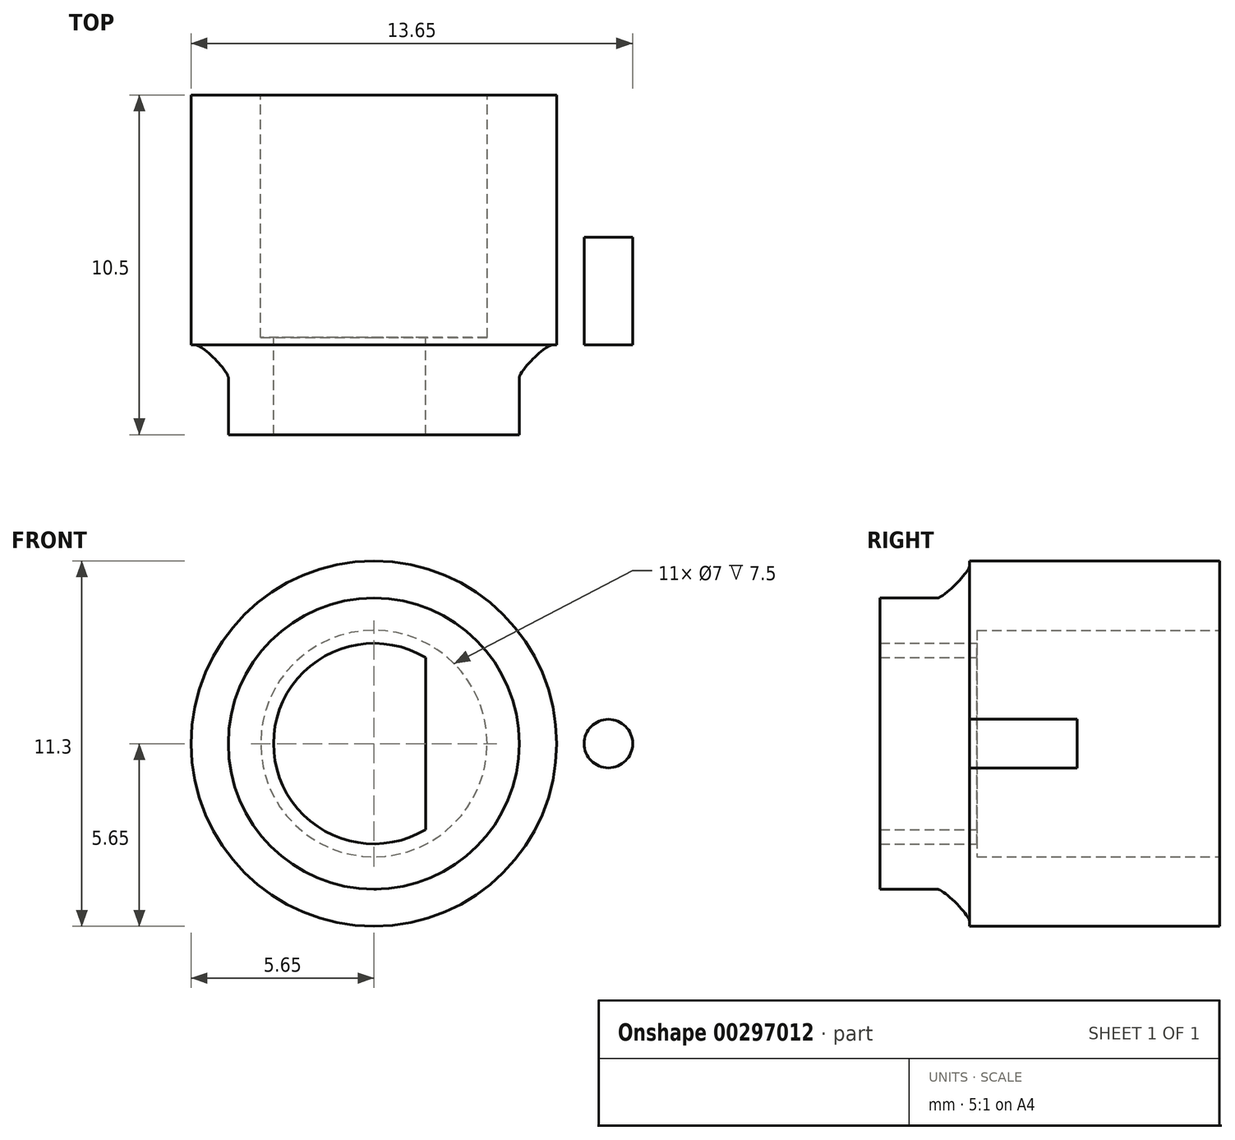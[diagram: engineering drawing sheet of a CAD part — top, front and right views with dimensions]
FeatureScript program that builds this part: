
annotation { "Feature Type Name" : "Feature", "Feature Type Description" : "" }
export const myFeature = defineFeature(function(context is Context, id is Id, definition is map)
    precondition{}
    {
        {
            var Q0;
            Q0=qCreatedBy(makeId("Top.planeOp"),FACE);
            var sketch = newSketch(context, id + "F0", { "sketchPlane" : qUnion([Q0])});
            skLineSegment(sketch, "E0", {"start": v(0, 7.73) * mm, "end": v(-5.65, 7.73) * mm});
            skLineSegment(sketch, "E1", {"start": v(-5.65, 7.73) * mm, "end": v(-5.65, 3.33) * mm});
            skLineSegment(sketch, "E2", {"start": v(-5.65, 3.33) * mm, "end": v(-9.35, 3.33) * mm});
            skLineSegment(sketch, "E3", {"start": v(-9.35, 3.33) * mm, "end": v(-9.35, 0) * mm});
            skLineSegment(sketch, "E4", {"start": v(-9.35, 0) * mm, "end": v(-4.5, 0) * mm});
            skLineSegment(sketch, "E5", {"start": v(-4.5, 0) * mm, "end": v(-4.5, -2.77) * mm});
            skLineSegment(sketch, "E6", {"start": v(-4.5, -2.77) * mm, "end": v(0, -2.77) * mm});
            skLineSegment(sketch, "E7", {"start": v(0, -2.77) * mm, "end": v(0, 7.73) * mm});
            skLineSegment(sketch, "E8", {"start": v(0, 7.73) * mm, "end": v(0, 5.8) * mm, "construction": true});
            skSolve(sketch);
        }
        {
            var Q0;
            {var subQ0=sQuery(id+"F0.wireOp",EDGE,"E0");Q0=makeQuery(id+"F0.imprint","IMPRINT",FACE,{"disambiguationData":[TD([[makeQuery(id+"F0.imprint","IMPRINT",EDGE,{"derivedFrom":subQ0}),1.0]])]});}
            var Q1;
            Q1=sQuery(id+"F0.wireOp",EDGE,"E7");
            revolve(context, id + "F1", {"entities" : qUnion([Q0]), "axis" : qUnion([Q1]), "revolveType" : RevolveType.FULL});
        }
        {
            var Q0;
            Q0=makeQuery(id+"F1.opRevolve","SWEPT_FACE",FACE,{"disambiguationData":[OSD([sQuery(id+"F0.wireOp",EDGE,"E2")])]});
            var sketch = newSketch(context, id + "F2", { "sketchPlane" : qUnion([Q0])});
            skLineSegment(sketch, "E9", {"start": v(0, 0) * mm, "end": v(-8, 0) * mm, "construction": true});
            skLineSegment(sketch, "E10", {"start": v(8, 0) * mm, "end": v(3.1, 0) * mm, "construction": true});
            skPoint(sketch, "E11", {"position": v(8, 0) * mm});
            skPoint(sketch, "E12", {"position": v(-8, 0) * mm});
            skPoint(sketch, "E13.orphan", {"position": v(9.35, 0) * mm});
            skCircle(sketch, "E14", {"center": v(7.25, 0) * mm, "radius": 0.75 * mm});
            skLineSegment(sketch, "E15", {"start": v(0, -5.65) * mm, "end": v(0, 5.65) * mm, "construction": true});
            skCircle(sketch, "E16.MirrorC", {"center": v(-7.25, 0) * mm, "radius": 0.75 * mm});
            skArc(sketch, "E17", {"start": v(-1.6, -2.66) * mm, "mid": v(3.1, 0) * mm, "end": v(-1.6, 2.66) * mm});
            skLineSegment(sketch, "E18", {"start": v(-1.6, 2.66) * mm, "end": v(-1.6, -2.66) * mm});
            skLineSegment(sketch, "E19", {"start": v(3.1, 0) * mm, "end": v(0, 0) * mm, "construction": true});
            skCircle(sketch, "E20", {"center": v(0, 0) * mm, "radius": 4.65 * mm});
            skSolve(sketch);
        }
        {
            var Q0;
            Q0=makeQuery(id+"F2.imprint","IMPRINT",FACE,{"disambiguationData":[TD([[makeQuery(id+"F2.imprint","IMPRINT",EDGE,{"derivedFrom":sQuery(id+"F2.wireOp",EDGE,"E14")}),1.0]])]});
            var Q1;
            Q1=makeQuery(id+"F2.imprint","IMPRINT",FACE,{"disambiguationData":[TD([[makeQuery(id+"F2.imprint","IMPRINT",EDGE,{"derivedFrom":sQuery(id+"F2.wireOp",EDGE,"E16.MirrorC")}),-1.0]])]});
            var Q2;
            Q2=sQuery(id+"F2.wireOp",EDGE,"E14");
            var Q3;
            Q3=sQuery(id+"F2.wireOp",EDGE,"E16.MirrorC");
            extrude(context, id + "F3", {"entities" : qUnion([Q0, Q1]), "operationType" : NewBodyOperationType.REMOVE, "surfaceEntities" : qUnion([Q2, Q3]), "endBound" : BoundingType.THROUGH_ALL, "oppositeDirection" : true, "depth" : 7.7 * mm});
        }
        {
            var Q0;
            Q0=makeQuery(id+"F2.imprint","IMPRINT",FACE,{"disambiguationData":[TD([[makeQuery(id+"F2.imprint","IMPRINT",EDGE,{"derivedFrom":sQuery(id+"F2.wireOp",EDGE,"E17")}),1.0]])]});
            extrude(context, id + "F4", {"entities" : qUnion([Q0]), "operationType" : NewBodyOperationType.REMOVE, "endBound" : BoundingType.THROUGH_ALL, "oppositeDirection" : true, "depth" : 25 * mm, "hasSecondDirection" : true, "secondDirectionBound" : SecondDirectionBoundingType.THROUGH_ALL, "secondDirectionOppositeDirection" : false, "secondDirectionDepth" : 25 * mm});
        }
        {
            var Q0;
            Q0=makeQuery(id+"F1.opRevolve","SWEPT_FACE",FACE,{"disambiguationData":[OSD([sQuery(id+"F0.wireOp",EDGE,"E0")])]});
            var sketch = newSketch(context, id + "F5", { "sketchPlane" : qUnion([Q0])});
            skPoint(sketch, "E21", {"position": v(0, 0) * mm});
            skCircle(sketch, "E22", {"center": v(0, 0) * mm, "radius": 3.5 * mm});
            skSolve(sketch);
        }
        {
            var Q0;
            Q0=makeQuery(id+"F5.imprint","IMPRINT",FACE,{"disambiguationData":[TD([[makeQuery(id+"F5.imprint","IMPRINT",EDGE,{"derivedFrom":sQuery(id+"F5.wireOp",EDGE,"E22")}),1.0]])]});
            var Q1;
            Q1=sQuery(id+"F5.wireOp",EDGE,"E22");
            extrude(context, id + "F6", {"entities" : qUnion([Q0]), "operationType" : NewBodyOperationType.REMOVE, "surfaceEntities" : qUnion([Q1]), "oppositeDirection" : true, "depth" : 7.5 * mm});
        }
        {
            var Q0;
            Q0=makeQuery(id+"F1.opRevolve","SWEPT_EDGE",EDGE,{"disambiguationData":[OSD([sQuery(id+"F0.wireOp",EDGE,"E4"),sQuery(id+"F0.wireOp",EDGE,"E5")])]});
            fillet(context, id + "F7", {"entities" : qUnion([Q0]), "radius" : 1 * mm, "tangentPropagation" : true, "rho" : .15, "crossSection" : FilletCrossSection.CONIC, "allowEdgeOverflow" : false});
        }
    });
